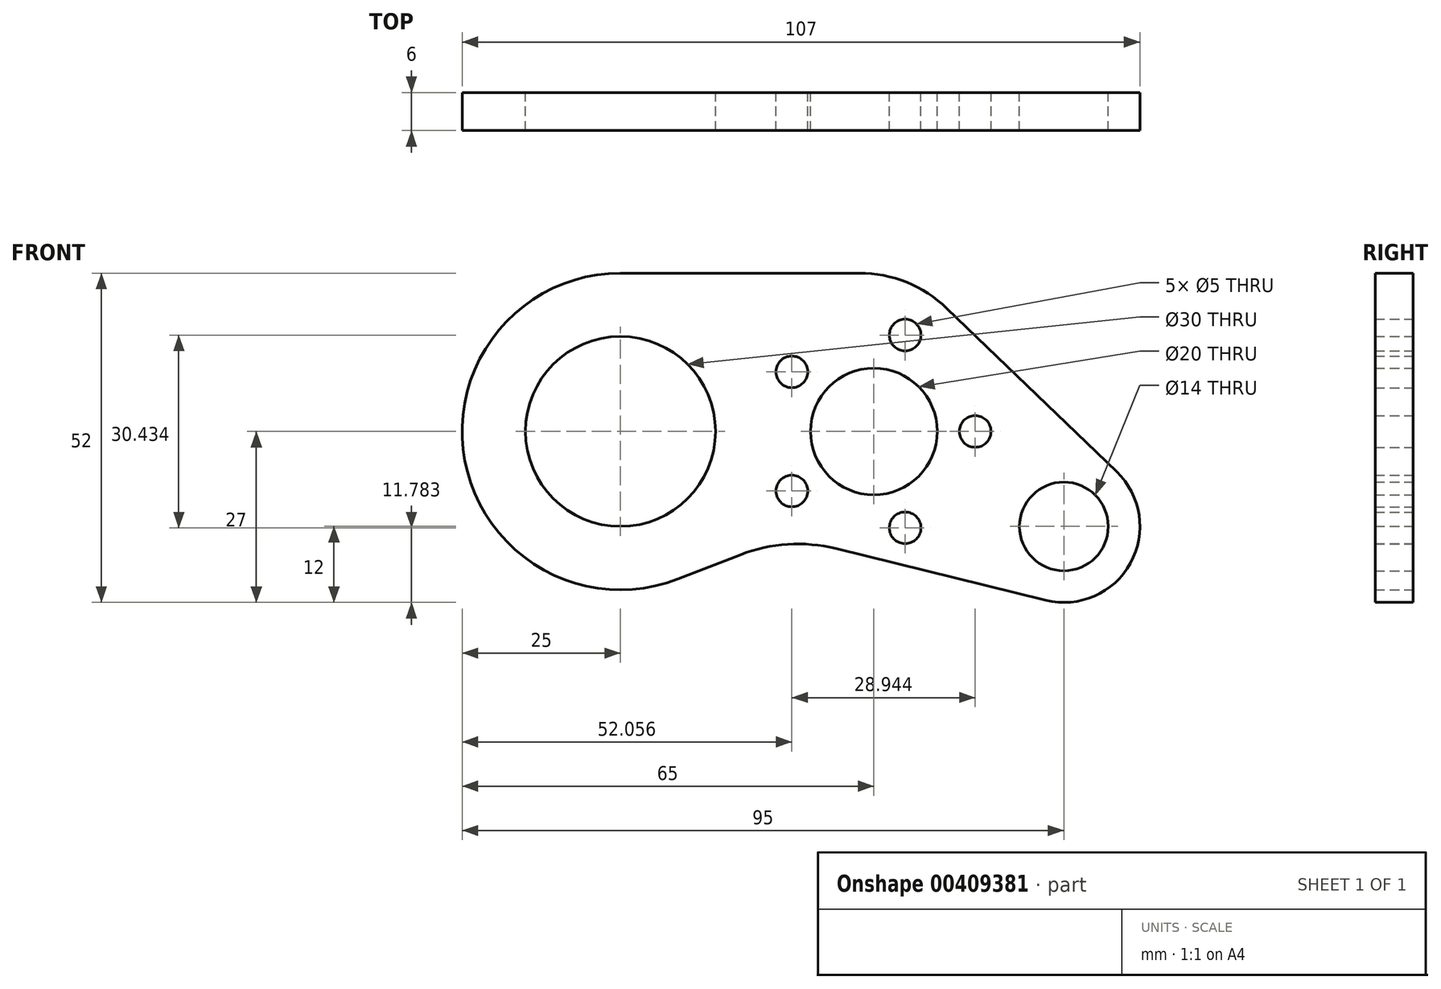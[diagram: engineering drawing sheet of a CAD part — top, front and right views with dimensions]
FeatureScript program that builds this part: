
annotation { "Feature Type Name" : "Feature", "Feature Type Description" : "" }
export const myFeature = defineFeature(function(context is Context, id is Id, definition is map)
    precondition{}
    {
        {
            var Q0;
            Q0=qCreatedBy(makeId("Front.planeOp"),FACE);
            var sketch = newSketch(context, id + "F0", { "sketchPlane" : qUnion([Q0])});
            skArc(sketch, "E0", {"start": v(0, 25) * mm, "mid": v(-24.57, -4.6) * mm, "end": v(9.04, -23.3) * mm});
            skCircle(sketch, "E1", {"center": v(0, 0) * mm, "radius": 15 * mm});
            skCircle(sketch, "E2", {"center": v(40, 0) * mm, "radius": 10 * mm});
            skCircle(sketch, "E3", {"center": v(70, -15) * mm, "radius": 7 * mm});
            skLineSegment(sketch, "E4", {"start": v(0, 25) * mm, "end": v(37.69, 25) * mm});
            skArc(sketch, "E5", {"start": v(67.13, -26.65) * mm, "mid": v(80.5, -20.8) * mm, "end": v(78.32, -6.36) * mm});
            skLineSegment(sketch, "E6", {"start": v(78.32, -6.36) * mm, "end": v(51.56, 19.4) * mm});
            skLineSegment(sketch, "E7", {"start": v(9.04, -23.3) * mm, "end": v(18.96, -19.46) * mm});
            skLineSegment(sketch, "E8", {"start": v(67.13, -26.65) * mm, "end": v(33.98, -18.5) * mm});
            skPoint(sketch, "E9.visualSharp", {"position": v(45.75, 25) * mm});
            skArc(sketch, "E9.filletArc", {"start": v(51.56, 19.4) * mm, "mid": v(45.17, 23.55) * mm, "end": v(37.69, 25) * mm});
            skPoint(sketch, "E10.visualSharp", {"position": v(26.32, -16.6) * mm});
            skArc(sketch, "E10.filletArc", {"start": v(33.98, -18.5) * mm, "mid": v(26.4, -17.82) * mm, "end": v(18.96, -19.46) * mm});
            skCircle(sketch, "E11", {"center": v(44.94, 15.22) * mm, "radius": 2.5 * mm});
            skLineSegment(sketch, "E12", {"start": v(40, 0) * mm, "end": v(44.94, 15.22) * mm, "construction": true});
            skCircle(sketch, "E13.1.0", {"center": v(27.06, 9.4) * mm, "radius": 2.5 * mm});
            skLineSegment(sketch, "E13.1.1", {"start": v(40, 0) * mm, "end": v(27.06, 9.4) * mm, "construction": true});
            skCircle(sketch, "E13.2.0", {"center": v(27.06, -9.4) * mm, "radius": 2.5 * mm});
            skLineSegment(sketch, "E13.2.1", {"start": v(40, 0) * mm, "end": v(27.06, -9.4) * mm, "construction": true});
            skCircle(sketch, "E13.3.0", {"center": v(44.94, -15.22) * mm, "radius": 2.5 * mm});
            skLineSegment(sketch, "E13.3.1", {"start": v(40, 0) * mm, "end": v(44.94, -15.22) * mm, "construction": true});
            skCircle(sketch, "E13.4.0", {"center": v(56, 0) * mm, "radius": 2.5 * mm});
            skLineSegment(sketch, "E13.4.1", {"start": v(40, 0) * mm, "end": v(56, 0) * mm, "construction": true});
            skSolve(sketch);
        }
        {
            var Q0;
            Q0=makeQuery(id+"F0.imprint","IMPRINT",FACE,{"disambiguationData":[TD([[makeQuery(id+"F0.imprint","IMPRINT",EDGE,{"derivedFrom":sQuery(id+"F0.wireOp",EDGE,"E0")}),1.0]])]});
            extrude(context, id + "F1", {"entities" : qUnion([Q0]), "depth" : 6 * mm});
        }
    });
